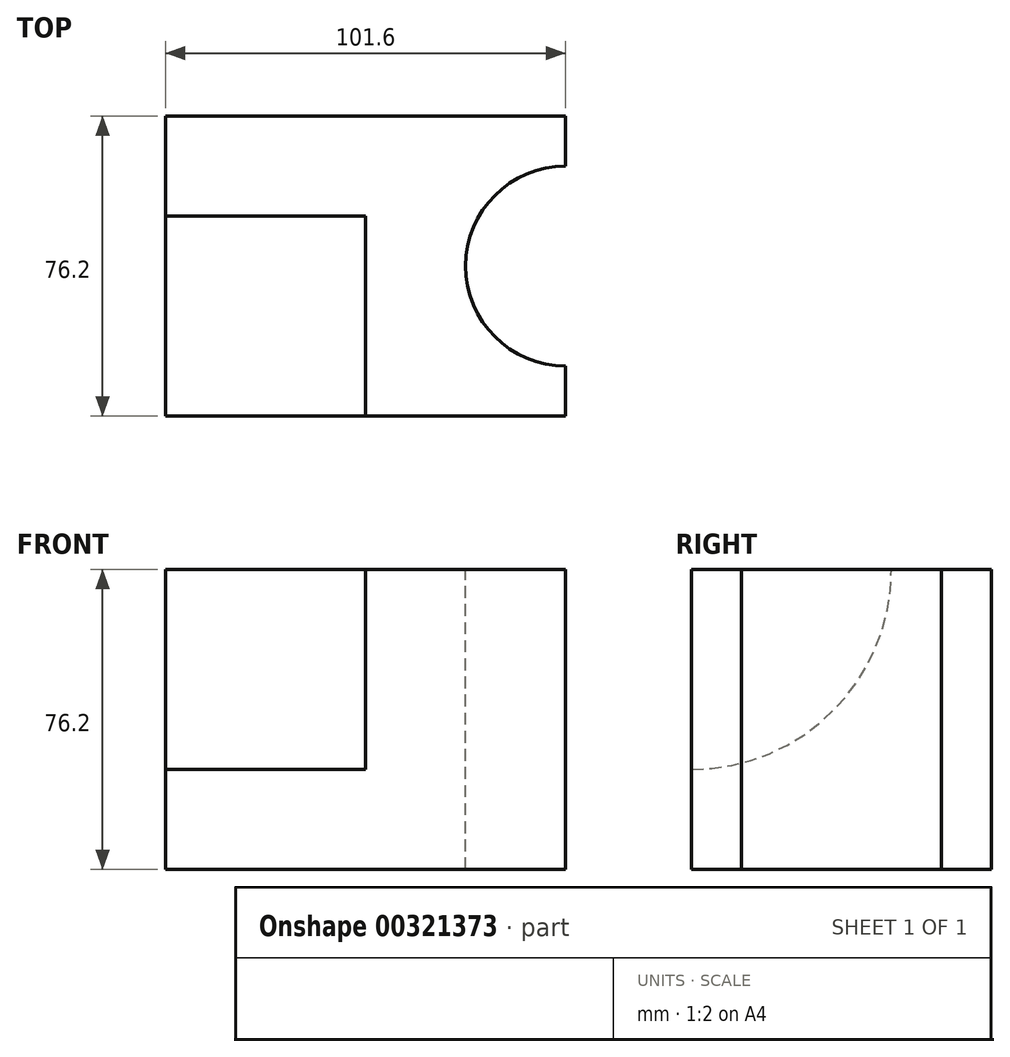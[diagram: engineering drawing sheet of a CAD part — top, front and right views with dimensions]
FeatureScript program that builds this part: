
annotation { "Feature Type Name" : "Feature", "Feature Type Description" : "" }
export const myFeature = defineFeature(function(context is Context, id is Id, definition is map)
    precondition{}
    {
        {
            var Q0;
            Q0=qCreatedBy(makeId("Front.planeOp"),FACE);
            var sketch = newSketch(context, id + "F0", { "sketchPlane" : qUnion([Q0])});
            skLineSegment(sketch, "E0.bottom", {"start": v(-29.33, 59.1) * mm, "end": v(72.27, 59.1) * mm});
            skLineSegment(sketch, "E0.top", {"start": v(-29.33, -17.1) * mm, "end": v(72.27, -17.1) * mm});
            skLineSegment(sketch, "E0.left", {"start": v(-29.33, 59.1) * mm, "end": v(-29.33, -17.1) * mm});
            skLineSegment(sketch, "E0.right", {"start": v(72.27, 59.1) * mm, "end": v(72.27, -17.1) * mm});
            skSolve(sketch);
        }
        {
            var Q0;
            Q0=makeQuery(id+"F0.imprint","IMPRINT",FACE,{"disambiguationData":[TD([[makeQuery(id+"F0.imprint","IMPRINT",EDGE,{"derivedFrom":sQuery(id+"F0.wireOp",EDGE,"E0.bottom")}),-1.0]])]});
            extrude(context, id + "F1", {"entities" : qUnion([Q0]), "depth" : 76.2 * mm});
        }
        {
            var Q0;
            Q0=makeQuery(id+"F1.opExtrude","SWEPT_FACE",FACE,{"disambiguationData":[OSD([sQuery(id+"F0.wireOp",EDGE,"E0.bottom")])]});
            var sketch = newSketch(context, id + "F2", { "sketchPlane" : qUnion([Q0])});
            skArc(sketch, "E1", {"start": v(72.27, -12.7) * mm, "mid": v(46.87, -38.1) * mm, "end": v(72.27, -63.5) * mm});
            skLineSegment(sketch, "E2", {"start": v(72.27, -12.7) * mm, "end": v(72.27, -63.5) * mm});
            skSolve(sketch);
        }
        {
            var Q0;
            Q0 = qSketchRegion(id + "F2", true);
            extrude(context, id + "F3", {"entities" : qUnion([Q0]), "operationType" : NewBodyOperationType.REMOVE, "endBound" : BoundingType.THROUGH_ALL, "oppositeDirection" : true, "depth" : 25.4 * mm});
        }
        {
            var Q0;
            Q0=makeQuery(id+"F1.opExtrude","SWEPT_FACE",FACE,{"disambiguationData":[OSD([sQuery(id+"F0.wireOp",EDGE,"E0.left")])]});
            var sketch = newSketch(context, id + "F4", { "sketchPlane" : qUnion([Q0])});
            skArc(sketch, "E3", {"start": v(25.4, 59.1) * mm, "mid": v(40.28, 23.18) * mm, "end": v(76.2, 8.3) * mm});
            skLineSegment(sketch, "E4", {"start": v(25.4, 59.1) * mm, "end": v(76.2, 59.1) * mm});
            skLineSegment(sketch, "E5", {"start": v(76.2, 59.1) * mm, "end": v(76.2, 8.3) * mm});
            skSolve(sketch);
        }
        {
            var Q0;
            Q0 = qSketchRegion(id + "F4", true);
            extrude(context, id + "F5", {"entities" : qUnion([Q0]), "operationType" : NewBodyOperationType.REMOVE, "oppositeDirection" : true, "depth" : 50.8 * mm});
        }
    });
